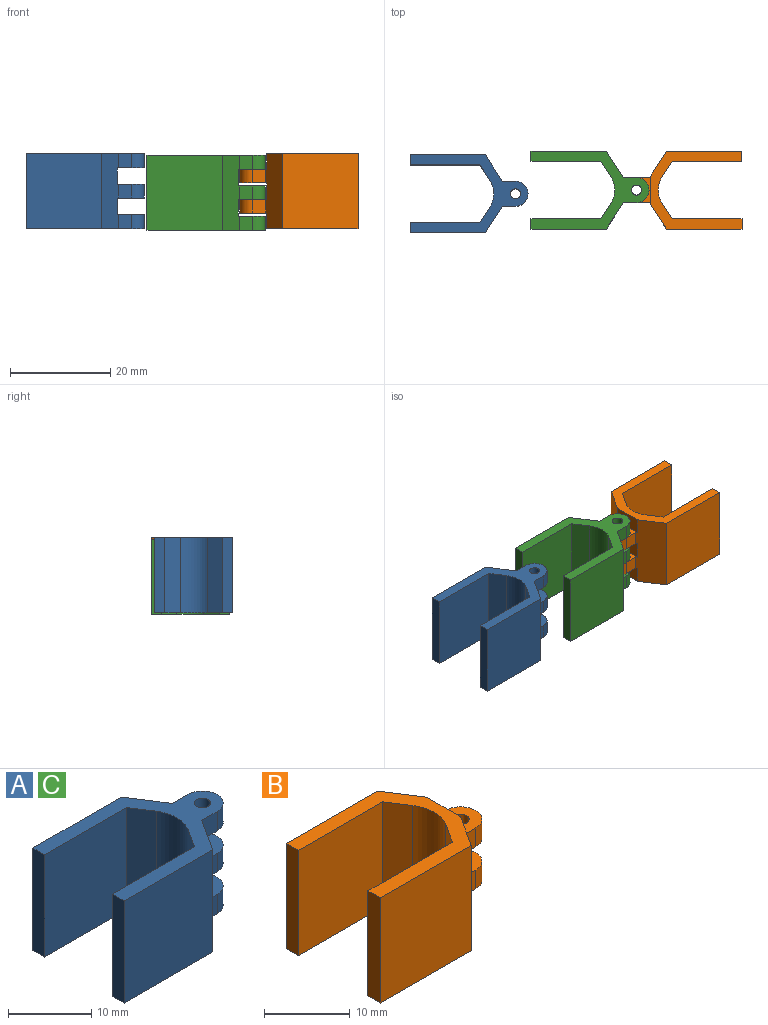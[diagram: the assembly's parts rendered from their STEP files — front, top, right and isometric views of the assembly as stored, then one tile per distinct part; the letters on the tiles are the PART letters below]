
ASSEMBLY  parts=3 mates=1
PART A: 31 faces, bbox 23.5x15.5x15 mm
  f0: plane 15x5.25mm, normal (0.84,-0.54,0), area 91.4mm2, adj f2,f3,f9,f20,f21,f22,f23,f24
  f1: plane 15x5.25mm, normal (0.84,0.54,0), area 91.4mm2, adj f4,f5,f11,f12,f21,f22,f23,f24
  f2: plane 2.85x2.61mm, normal (0,-1,0), area 7.4mm2, adj f0,f10,f22,f27
  f3: plane 2.7x2.61mm, normal (0,-1,0), area 7.1mm2, adj f0,f6,f23,f28
  f4: plane 2.85x2.61mm, normal (0,1,0), area 7.4mm2, adj f1,f10,f22,f27
  f5: plane 2.7x2.61mm, normal (0,1,0), area 7.1mm2, adj f1,f6,f23,f28
  f6: cylinder r=2.5mm len=5mm, axis (0,0,-1), area 21.2mm2, adj f3,f5,f23,f28
  f7: cylinder r=2.5mm len=5mm, axis (0,0,-1), area 22.4mm2, adj f9,f11,f21,f24
  f8: cylinder r=1mm len=2.85mm, axis (0,0,-1), area 17.9mm2, adj f21,f24
  f9: plane 2.85x2.61mm, normal (0,-1,0), area 7.4mm2, adj f0,f7,f21,f24
  f10: cylinder r=2.5mm len=5mm, axis (0,0,-1), area 22.4mm2, adj f2,f4,f22,f27
  f11: plane 2.85x2.61mm, normal (0,1,0), area 7.4mm2, adj f1,f7,f21,f24
  f12: plane 15x15mm, normal (0,1,0), area 225mm2, adj f1,f13,f21,f22
  f13: plane 15x2mm, normal (-1,0,0), area 30mm2, adj f12,f14,f21,f22
  f14: plane 15x13.91mm, normal (0,-1,0), area 208.7mm2, adj f13,f15,f21,f22
  f15: plane 15x3.04mm, normal (-0.84,-0.54,0), area 54.3mm2, adj f14,f21,f22,f30
  f16: plane 15x3.04mm, normal (-0.84,0.54,0), area 54.3mm2, adj f17,f21,f22,f30
  f17: plane 15x13.91mm, normal (0,1,0), area 208.7mm2, adj f16,f18,f21,f22
  f18: plane 15x2mm, normal (-1,0,0), area 30mm2, adj f17,f20,f21,f22
  f19: cylinder r=1mm len=2.85mm, axis (0,0,-1), area 17.9mm2, adj f22,f27
  f20: plane 15x15mm, normal (0,-1,0), area 225mm2, adj f0,f18,f21,f22
  f21: plane 23.5x15.5mm, normal (0,0,1), area 107.5mm2, adj f0,f1,f7,f8,f9,f11,f12,f13
  f22: plane 23.5x15.5mm, normal (0,0,-1), area 107.5mm2, adj f0,f1,f2,f4,f10,f12,f13,f14
  f23: plane 5.58x5.3mm, normal (0,0,1), area 20.7mm2, adj f0,f1,f3,f5,f6,f25,f26
  f24: plane 5.58x5.3mm, normal (0,0,-1), area 20.7mm2, adj f0,f1,f7,f8,f9,f11,f25
  f25: plane 5.58x3.3mm, normal (1,0,0), area 18.4mm2, adj f0,f1,f23,f24
  f26: cylinder r=1mm len=2.7mm, axis (0,0,-1), area 17mm2, adj f23,f28
  f27: plane 5.58x5.3mm, normal (0,0,1), area 20.7mm2, adj f0,f1,f2,f4,f10,f19,f29
  f28: plane 5.58x5.3mm, normal (0,0,-1), area 20.7mm2, adj f0,f1,f3,f5,f6,f26,f29
  f29: plane 5.58x3.3mm, normal (1,0,0), area 18.4mm2, adj f0,f1,f27,f28
  f30: cylinder r=5mm len=15mm, axis (0,0,1), area 85.9mm2, adj f15,f16,f21,f22
PART B: 28 faces, bbox 23.5x15.5x15 mm
  f0: plane 18.2x15.5mm, normal (0,0,1), area 86.7mm2, adj f1,f3,f10,f11,f12,f13,f14,f15
  f1: plane 15x5.25mm, normal (0.84,-0.54,0), area 90.4mm2, adj f0,f2,f4,f5,f17,f18,f19,f20
  f2: plane 18.2x15.5mm, normal (0,0,-1), area 86.7mm2, adj f1,f3,f10,f11,f12,f13,f14,f15
  f3: plane 15x5.25mm, normal (0.84,0.54,0), area 90.4mm2, adj f0,f2,f6,f7,f10,f18,f19,f20
  f4: plane 2.7x2.61mm, normal (0,-1,0), area 7.1mm2, adj f1,f9,f20,f23
  f5: plane 2.7x2.61mm, normal (0,-1,0), area 7.1mm2, adj f1,f8,f18,f24
  f6: plane 2.7x2.61mm, normal (0,1,0), area 7.1mm2, adj f3,f9,f20,f23
  f7: plane 2.7x2.61mm, normal (0,1,0), area 7.1mm2, adj f3,f8,f18,f24
  f8: cylinder r=2.5mm len=5mm, axis (0,0,-1), area 21.2mm2, adj f5,f7,f18,f24
  f9: cylinder r=2.5mm len=5mm, axis (0,0,-1), area 21.2mm2, adj f4,f6,f20,f23
  f10: plane 15x15mm, normal (0,1,0), area 225mm2, adj f0,f2,f3,f11
  f11: plane 15x2mm, normal (-1,0,0), area 30mm2, adj f0,f2,f10,f12
  f12: plane 15x13.91mm, normal (0,-1,0), area 208.7mm2, adj f0,f2,f11,f13
  f13: plane 15x3.04mm, normal (-0.84,-0.54,0), area 54.3mm2, adj f0,f2,f12,f27
  f14: plane 15x3.04mm, normal (-0.84,0.54,0), area 54.3mm2, adj f0,f2,f15,f27
  f15: plane 15x13.91mm, normal (0,1,0), area 208.7mm2, adj f0,f2,f14,f16
  f16: plane 15x2mm, normal (-1,0,0), area 30mm2, adj f0,f2,f15,f17
  f17: plane 15x15mm, normal (0,-1,0), area 225mm2, adj f0,f1,f2,f16
  f18: plane 5.58x5.3mm, normal (0,0,-1), area 20.7mm2, adj f1,f3,f5,f7,f8,f19,f22
  f19: plane 5.58x3.15mm, normal (1,0,0), area 17.6mm2, adj f1,f2,f3,f18
  f20: plane 5.58x5.3mm, normal (0,0,1), area 20.7mm2, adj f1,f3,f4,f6,f9,f21,f26
  f21: plane 5.58x3.15mm, normal (1,0,0), area 17.6mm2, adj f0,f1,f3,f20
  f22: cylinder r=1mm len=2.7mm, axis (0,0,-1), area 17mm2, adj f18,f24
  f23: plane 5.58x5.3mm, normal (0,0,-1), area 20.7mm2, adj f1,f3,f4,f6,f9,f25,f26
  f24: plane 5.58x5.3mm, normal (0,0,1), area 20.7mm2, adj f1,f3,f5,f7,f8,f22,f25
  f25: plane 5.58x3.3mm, normal (1,0,0), area 18.4mm2, adj f1,f3,f23,f24
  f26: cylinder r=1mm len=2.7mm, axis (0,0,-1), area 17mm2, adj f20,f23
  f27: cylinder r=5mm len=15mm, axis (0,0,1), area 85.9mm2, adj f0,f2,f13,f14
PART C: same geometry as A
PLACE A t=(-6.66,-0.35,-3.77)mm
PLACE B rot(axis=(0,0,-1),180deg) t=(39.42,0.38,-3.77)mm
PLACE C t=(17.42,0.38,-4.07)mm
MATE revolute C.f8 <-> B.f22  axis (0,0,-1) through (28.42,0.38,8.08)mm
